# Revit family: Caspian LST 90 Mk1
name_source: partatom
category: Mechanical Equipment
revit_build: Autodesk Revit 2017 (Build: 20160225_1515(x64)
units: mm (PartAtom-declared; Revit-internal decimal feet)

## family parameters
Always vertical = Yes
Cut with Voids When Loaded = No
Host = Wall
OmniClass Number = 23.75.00.00
OmniClass Title = Climate Control (HVAC)
Part Type = Normal
Room Calculation Point = No
Round Connector Dimension = Use Diameter
Shared = No

## types (1)
- Type 1
    Accessories = <By Category>
    Assembly Code = D3020300
    Color = Polyester powdercoated: White RAL 9010
    Data Sheet = http://smithsep.co.uk
    Description = One heating solution for a variety of applications - suitable for high, low or ceilingmounted
installation, you can even turn it upside down.
    Finish = Zinc-coated steel 1.2mm.
    Installation Guide = http://smithsep.co.uk
    Manufacturer = Smiths Enviromental Products LTD
    ManufacturerURL = http://www.smithsep.co.uk
    Model = Caspian UV 60 MK1
    NBSReference = T90 Heating systems
    NominalHeight = 0 mm  [stored 0 ft]
    NominalLength = 0 mm  [stored 0 ft]
    NominalWidth = 0 mm  [stored 0 ft]
    Revision = Rev1 - October 2016
    Specification = <By Category>
    URL = http://smithsep.co.uk
    Uniclass2015Reference = Ss_60_40_37_51
    WarrantyDescription = 5 years from date of purchase

note: [stored X ft] marks values corroborated as IEEE doubles in the binary element streams (Revit-internal decimal feet)

## geometry (parser evidence)
native form markers: Sweep x3
no freeform markers — native parametric forms only
